# Revit family: Windows_Hajom_Architect-Gen-2_Type-FH
name_source: partatom
category: Windows
units: mm (PartAtom-declared; Revit-internal decimal feet)

## family parameters
Always vertical = Yes
Cut with Voids When Loaded = No
Host = Wall
OmniClass Number = 23.30.20.00
Room Calculation Point = No
Shared = No

## types (1)
- Architect Gen 2 - Type FH (88-37-FH)
    AssetType = Fixed
    BIMObjectName = Windows_Hajom_Architect-Gen-2_Type-FH
    Brand = Hajom
    Category = Windows
    Default Sill Height = 800 mm  [stored 2.62467 ft]
    DoorMainMaterial = RAL9003-White-Internal_face
    DoorSecondaryMaterial = RAL7012-Basalt_Grey-External_face
    DurationUnit = Year
    Height = 0 mm  [stored 0 ft]
    Manufacturer = Hajom
    ManufacturerName = Hajom
    ManufacturerURL = https://www.hajom.com
    Material = Wood
    Model = Architect Gen 2 - Type FH (88-37-FH)
    NBSDescription = Wood window units
    NBSReference = 45-25-99/350
    Name = Architect-Gen-2_Type-FH
    NominalDepth = 215 mm
    Shape = Rectangular
    Size = 1580-4780x1780-2820x215 mm
    URL = https://www.hajom.com
    Uniclass2 = Pr_30_59_98
    Uniclass2015Description = Wood window units
    Uniclass2015Reference = Pr_30_59_98_96
    Version = 1
    VersionDate = 18/08/2025
    Wall Closure = By host
    WarrantyDurationUnit = Year
    Width = 0 mm  [stored 0 ft]

note: [stored X ft] marks values corroborated as IEEE doubles in the binary element streams (Revit-internal decimal feet)

## geometry (parser evidence)
native form markers: Sweep x8
no freeform markers — native parametric forms only
